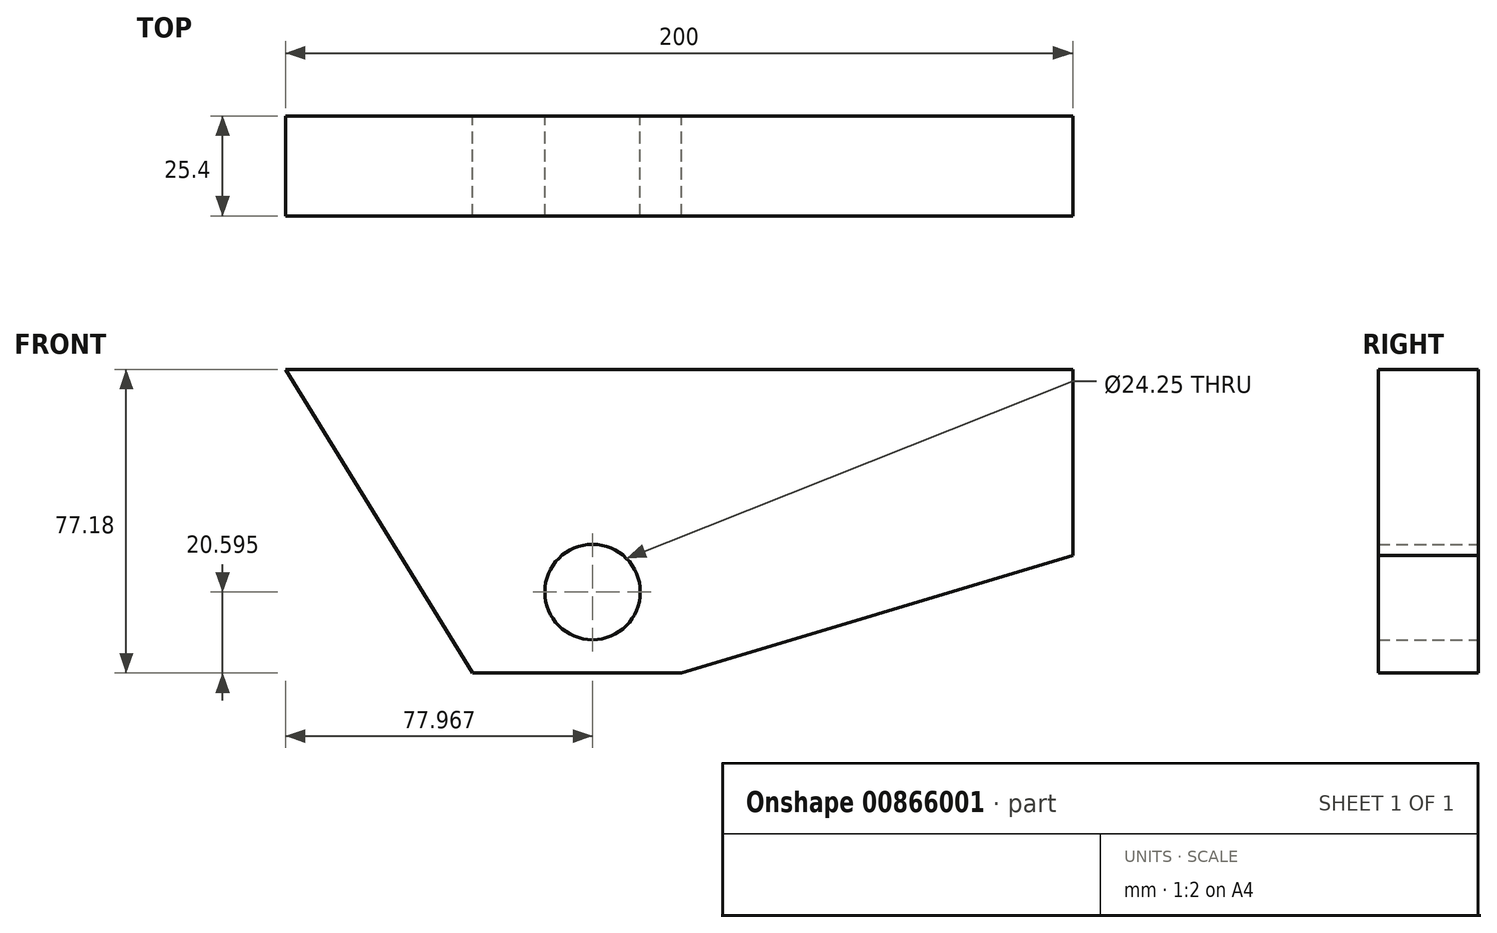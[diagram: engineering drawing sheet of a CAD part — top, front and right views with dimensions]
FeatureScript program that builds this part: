
annotation { "Feature Type Name" : "Feature", "Feature Type Description" : "" }
export const myFeature = defineFeature(function(context is Context, id is Id, definition is map)
    precondition{}
    {
        {
            var Q0;
            Q0=qCreatedBy(makeId("Front.planeOp"),FACE);
            var sketch = newSketch(context, id + "F0", { "sketchPlane" : qUnion([Q0])});
            skLineSegment(sketch, "E0", {"start": v(-203.45, 84.92) * mm, "end": v(-2.97, 84.92) * mm});
            skLineSegment(sketch, "E1", {"start": v(-2.97, 84.92) * mm, "end": v(-2.97, 37.57) * mm});
            skLineSegment(sketch, "E2", {"start": v(-2.97, 37.57) * mm, "end": v(-102.4, 7.74) * mm});
            skLineSegment(sketch, "E3", {"start": v(-102.4, 7.74) * mm, "end": v(-155.51, 7.74) * mm});
            skLineSegment(sketch, "E4", {"start": v(-155.51, 7.74) * mm, "end": v(-202.97, 84.92) * mm});
            skCircle(sketch, "E5", {"center": v(-125, 28.33) * mm, "radius": 12.12 * mm});
            skSolve(sketch);
        }
        {
            var Q0;
            Q0=makeQuery(id+"F0.imprint","IMPRINT",FACE,{"disambiguationData":[TD([[makeQuery(id+"F0.imprint","IMPRINT",EDGE,{"derivedFrom":sQuery(id+"F0.wireOp",EDGE,"E0")}),-1.0]])]});
            extrude(context, id + "F1", {"entities" : qUnion([Q0]), "depth" : 25.4 * mm, "offsetDistance" : 25.4 * mm});
        }
    });
